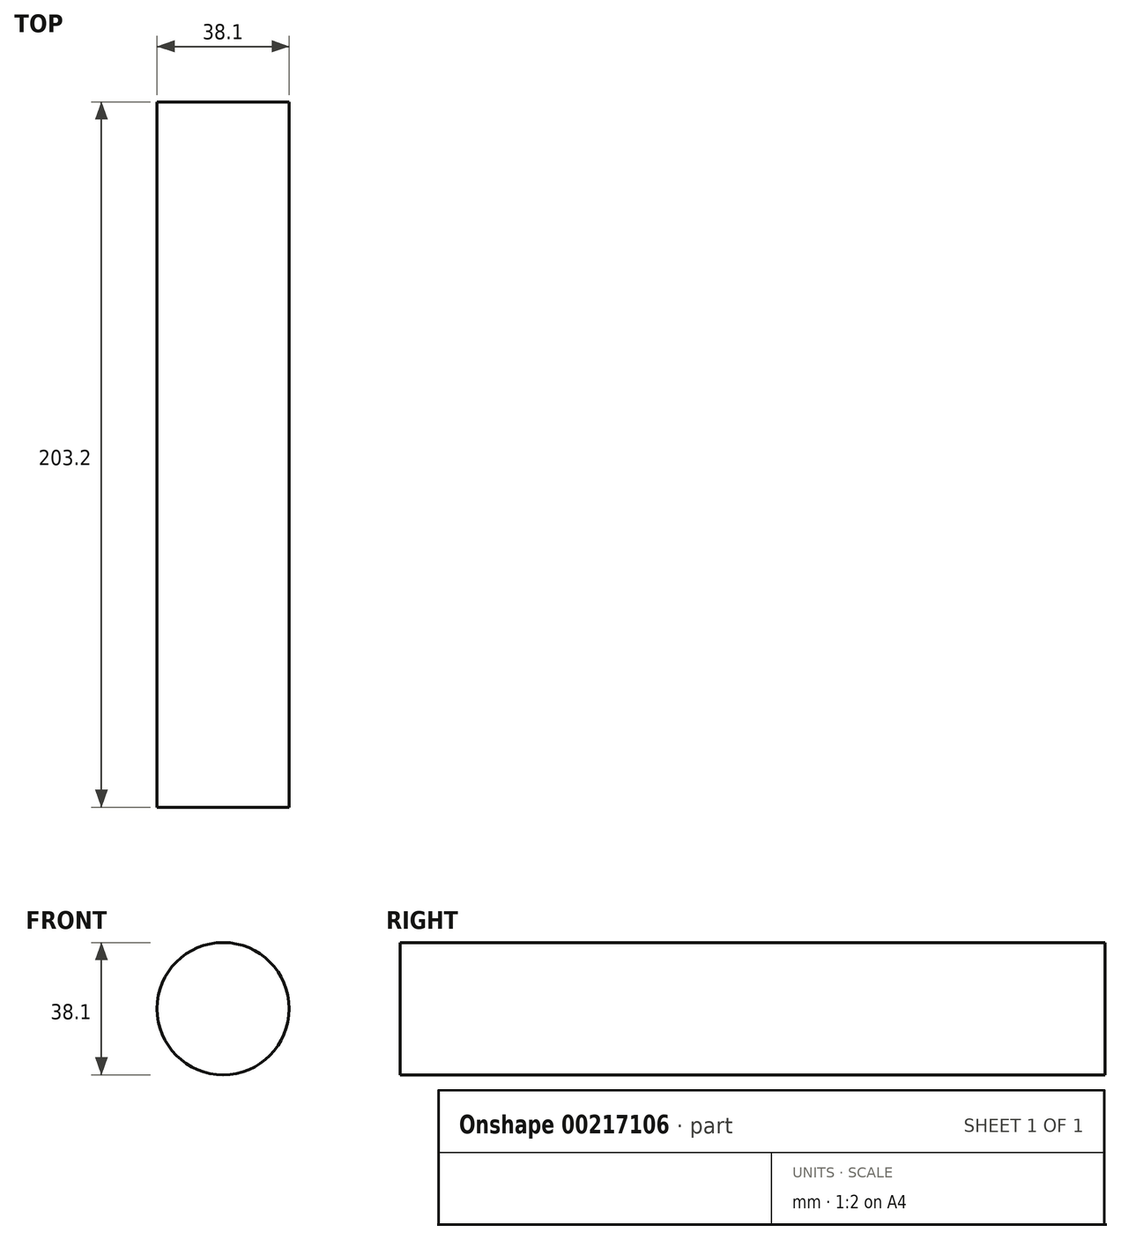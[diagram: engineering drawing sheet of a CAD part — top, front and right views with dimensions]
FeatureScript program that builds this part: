
annotation { "Feature Type Name" : "Feature", "Feature Type Description" : "" }
export const myFeature = defineFeature(function(context is Context, id is Id, definition is map)
    precondition{}
    {
        {
            var Q0;
            Q0=qCreatedBy(makeId("Front.planeOp"),FACE);
            var sketch = newSketch(context, id + "F0", { "sketchPlane" : qUnion([Q0])});
            skCircle(sketch, "E0", {"center": v(0, 0) * mm, "radius": 19.05 * mm});
            skCircle(sketch, "E1", {"center": v(0, 0) * mm, "radius": 15.88 * mm});
            skSolve(sketch);
        }
        {
            var Q0;
            Q0 = qSketchRegion(id + "F0", true);
            var Q1;
            Q1=makeQuery(id+"F0.imprint","IMPRINT",FACE,{"disambiguationData":[TD([[makeQuery(id+"F0.imprint","IMPRINT",EDGE,{"derivedFrom":sQuery(id+"F0.wireOp",EDGE,"E1")}),1.0]])]});
            extrude(context, id + "F1", {"entities" : qUnion([Q0, Q1]), "depth" : 203.2 * mm});
        }
        {
            var Q0;
            Q0=makeQuery(id+"F1.opExtrude","CAP_FACE",FACE,{"disambiguationData":[OSD([sQuery(id+"F0.wireOp",EDGE,"E0")])],"isStart":true});
            extrude(context, id + "F2", {"entities" : qUnion([Q0]), "operationType" : NewBodyOperationType.REMOVE, "oppositeDirection" : true, "depth" : 25.4 * mm});
        }
        {
            var Q0;
            Q0=makeQuery(id+"F2.boolean.opBoolean","COPY",FACE,{"derivedFrom":makeQuery(id+"F2.opExtrude","CAP_FACE",FACE,{"disambiguationData":[OSD([sQuery(id+"F0.wireOp",EDGE,"E0")])],"isStart":false})});
            extrude(context, id + "F3", {"entities" : qUnion([Q0]), "operationType" : NewBodyOperationType.ADD, "depth" : 25.4 * mm});
        }
    });
